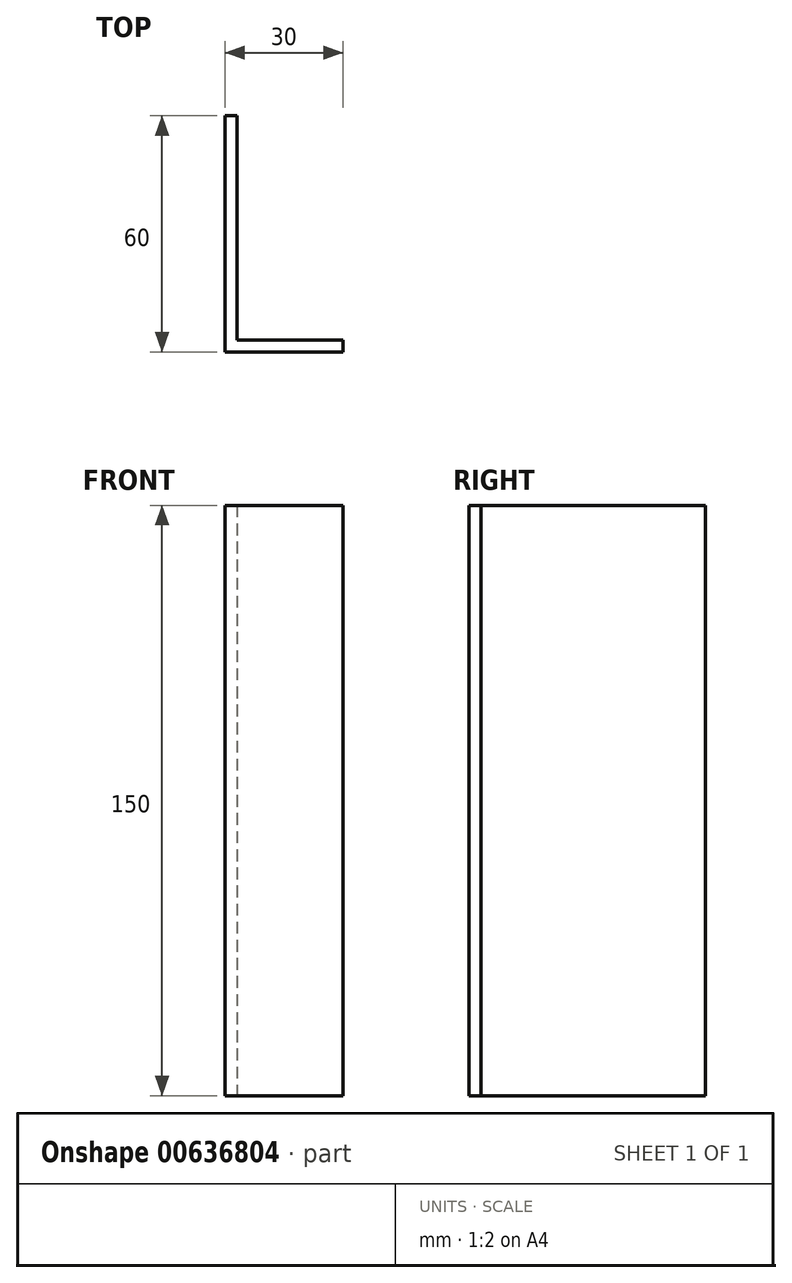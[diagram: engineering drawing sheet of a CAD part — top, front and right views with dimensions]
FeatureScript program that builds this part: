
annotation { "Feature Type Name" : "Feature", "Feature Type Description" : "" }
export const myFeature = defineFeature(function(context is Context, id is Id, definition is map)
    precondition{}
    {
        {
            var Q0;
            Q0=qCreatedBy(makeId("Top.planeOp"),FACE);
            var sketch = newSketch(context, id + "F0", { "sketchPlane" : qUnion([Q0])});
            skLineSegment(sketch, "E0", {"start": v(0, 0) * mm, "end": v(0, 60) * mm});
            skLineSegment(sketch, "E1", {"start": v(0, 60) * mm, "end": v(3, 60) * mm});
            skLineSegment(sketch, "E2", {"start": v(3, 60) * mm, "end": v(3, 3) * mm});
            skLineSegment(sketch, "E3", {"start": v(3, 3) * mm, "end": v(30, 3) * mm});
            skLineSegment(sketch, "E4", {"start": v(30, 3) * mm, "end": v(30, 3) * mm});
            skLineSegment(sketch, "E5", {"start": v(30, 0) * mm, "end": v(30, 3) * mm});
            skLineSegment(sketch, "E6", {"start": v(30, 0) * mm, "end": v(0, 0) * mm});
            skSolve(sketch);
        }
        {
            var Q0;
            Q0=makeQuery(id+"F0.imprint","IMPRINT",FACE,{"disambiguationData":[TD([[makeQuery(id+"F0.imprint","IMPRINT",EDGE,{"derivedFrom":sQuery(id+"F0.wireOp",EDGE,"E0")}),-1.0]])]});
            extrude(context, id + "F1", {"entities" : qUnion([Q0]), "depth" : 150 * mm, "offsetDistance" : 25 * mm});
        }
    });
